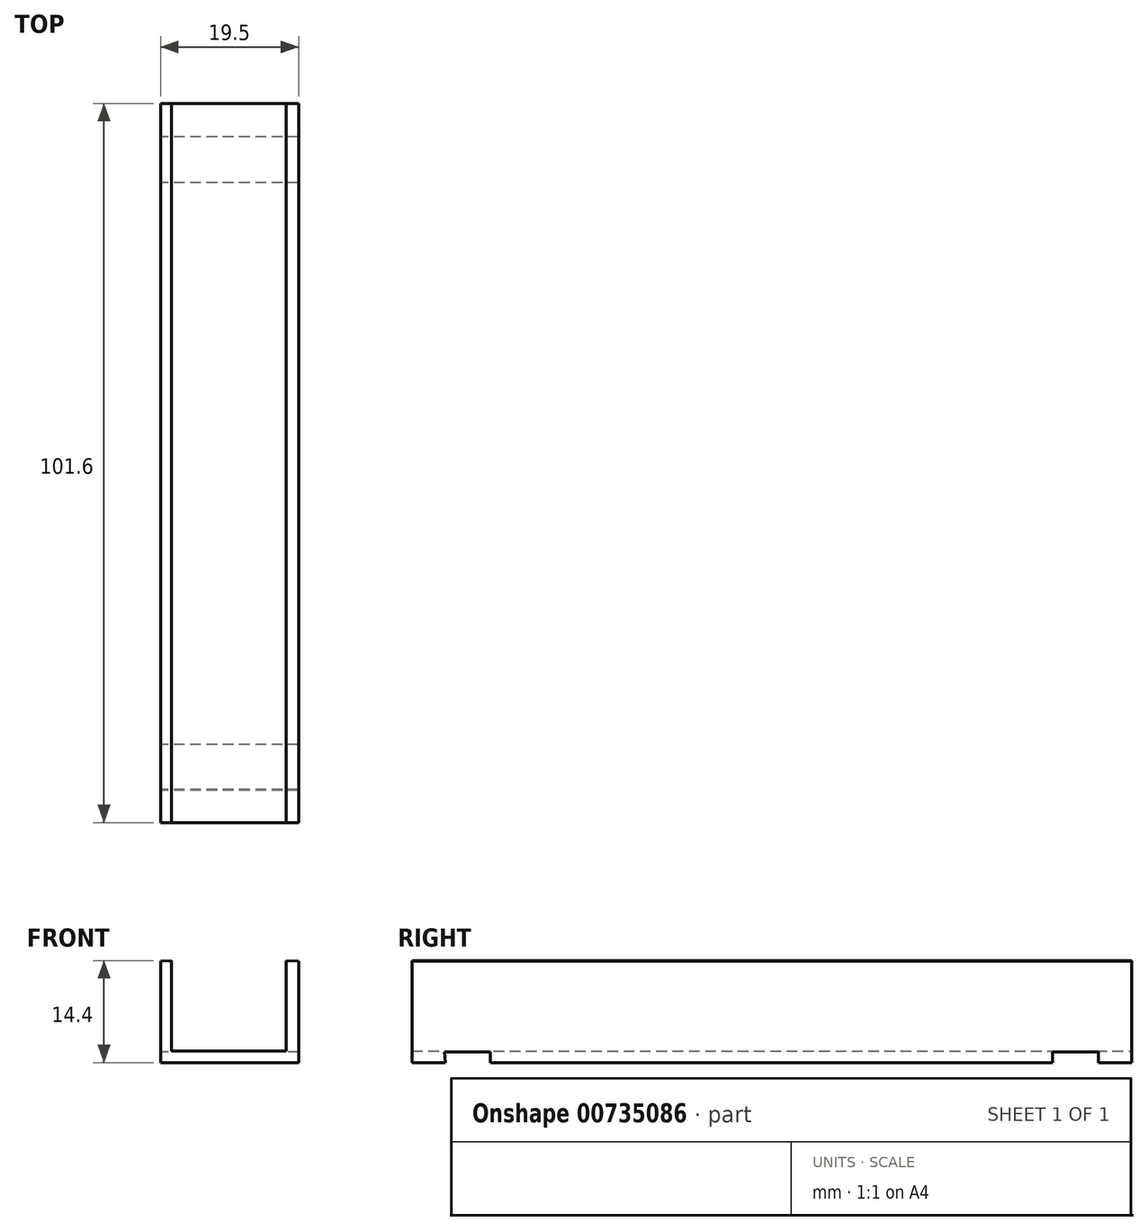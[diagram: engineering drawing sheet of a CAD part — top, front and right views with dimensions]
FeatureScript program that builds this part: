
annotation { "Feature Type Name" : "Feature", "Feature Type Description" : "" }
export const myFeature = defineFeature(function(context is Context, id is Id, definition is map)
    precondition{}
    {
        {
            var Q0;
            Q0=qCreatedBy(makeId("Front.planeOp"),FACE);
            var sketch = newSketch(context, id + "F0", { "sketchPlane" : qUnion([Q0])});
            skLineSegment(sketch, "E0.bottom", {"start": v(0, 0) * mm, "end": v(19.5, 0) * mm});
            skLineSegment(sketch, "E0.left", {"start": v(0, 0) * mm, "end": v(0, 14.34) * mm});
            skLineSegment(sketch, "E0.right", {"start": v(19.5, 0) * mm, "end": v(19.5, 14.34) * mm});
            skLineSegment(sketch, "E1.bottom", {"start": v(1.55, 1.62) * mm, "end": v(17.73, 1.62) * mm});
            skLineSegment(sketch, "E1.left", {"start": v(1.55, 1.62) * mm, "end": v(1.55, 14.4) * mm});
            skLineSegment(sketch, "E1.right", {"start": v(17.73, 1.62) * mm, "end": v(17.73, 14.4) * mm});
            skLineSegment(sketch, "E2", {"start": v(0, 14.34) * mm, "end": v(1.55, 14.4) * mm});
            skLineSegment(sketch, "E3", {"start": v(17.73, 14.4) * mm, "end": v(19.5, 14.34) * mm});
            skSolve(sketch);
        }
        {
            var Q0;
            Q0=makeQuery(id+"F0.imprint","IMPRINT",FACE,{"disambiguationData":[TD([[makeQuery(id+"F0.imprint","IMPRINT",EDGE,{"derivedFrom":sQuery(id+"F0.wireOp",EDGE,"E0.bottom")}),1.0]])]});
            extrude(context, id + "F1", {"entities" : qUnion([Q0]), "depth" : 101.6 * mm, "offsetDistance" : 25.4 * mm});
        }
        {
            var Q0;
            Q0=makeQuery(id+"F1.opExtrude","SWEPT_FACE",FACE,{"disambiguationData":[OSD([sQuery(id+"F0.wireOp",EDGE,"E0.left")])]});
            var sketch = newSketch(context, id + "F2", { "sketchPlane" : qUnion([Q0])});
            skLineSegment(sketch, "E4.bottom", {"start": v(4.7, 0) * mm, "end": v(11.18, 0) * mm});
            skLineSegment(sketch, "E4.top", {"start": v(4.7, 1.5) * mm, "end": v(11.18, 1.5) * mm});
            skLineSegment(sketch, "E4.left", {"start": v(4.7, 0) * mm, "end": v(4.7, 1.5) * mm});
            skLineSegment(sketch, "E4.right", {"start": v(11.18, 0) * mm, "end": v(11.18, 1.5) * mm});
            skLineSegment(sketch, "E5.MirrorCS", {"start": v(90.55, 0) * mm, "end": v(90.55, 1.5) * mm});
            skLineSegment(sketch, "E6.MirrorCS", {"start": v(96.9, 0) * mm, "end": v(97.03, 1.5) * mm});
            skLineSegment(sketch, "E7.MirrorCS", {"start": v(96.9, 0) * mm, "end": v(90.55, 0) * mm});
            skLineSegment(sketch, "E8.MirrorCS", {"start": v(97.03, 1.5) * mm, "end": v(90.55, 1.5) * mm});
            skSolve(sketch);
        }
        {
            var Q0;
            Q0 = qSketchRegion(id + "F2", true);
            extrude(context, id + "F3", {"entities" : qUnion([Q0]), "operationType" : NewBodyOperationType.REMOVE, "endBound" : BoundingType.UP_TO_NEXT, "oppositeDirection" : true, "depth" : -25.4 * mm, "offsetDistance" : -12.7 * mm});
        }
    });
